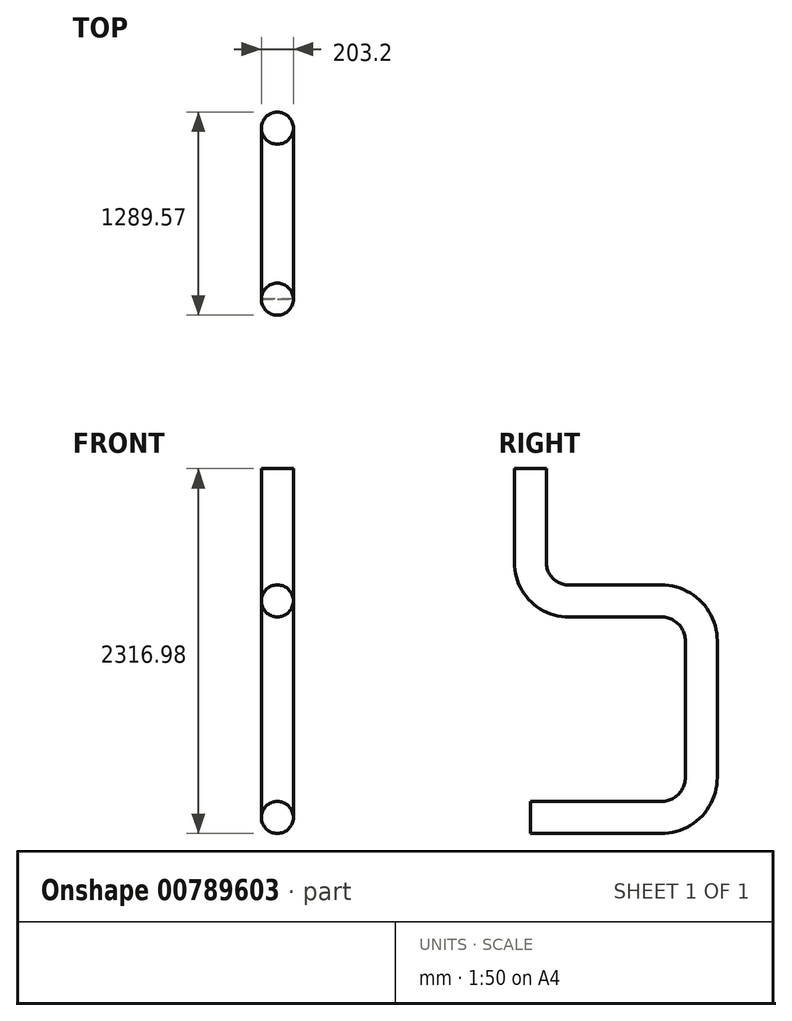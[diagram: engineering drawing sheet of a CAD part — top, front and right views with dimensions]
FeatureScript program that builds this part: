
annotation { "Feature Type Name" : "Feature", "Feature Type Description" : "" }
export const myFeature = defineFeature(function(context is Context, id is Id, definition is map)
    precondition{}
    {
        {
            var Q0;
            Q0=qCreatedBy(makeId("Front.planeOp"),FACE);
            var sketch = newSketch(context, id + "F0", { "sketchPlane" : qUnion([Q0])});
            skCircle(sketch, "E0", {"center": v(0, 0) * mm, "radius": 101.6 * mm});
            skSolve(sketch);
        }
        {
            var Q0;
            Q0=qCreatedBy(makeId("Right.planeOp"),FACE);
            var sketch = newSketch(context, id + "F1", { "sketchPlane" : qUnion([Q0])});
            skLineSegment(sketch, "E1", {"start": v(0, 0) * mm, "end": v(832.37, 0) * mm});
            skLineSegment(sketch, "E2", {"start": v(1086.37, 254) * mm, "end": v(1086.37, 1121.24) * mm});
            skArc(sketch, "E3", {"start": v(832.37, 0) * mm, "mid": v(1011.97, 74.4) * mm, "end": v(1086.37, 254) * mm});
            skPoint(sketch, "E3.first.point", {"position": v(1086.37, 254) * mm});
            skLineSegment(sketch, "E4", {"start": v(832.37, 1375.24) * mm, "end": v(244.31, 1375.24) * mm});
            skArc(sketch, "E5", {"start": v(1086.37, 1121.24) * mm, "mid": v(1011.97, 1300.85) * mm, "end": v(832.37, 1375.24) * mm});
            skPoint(sketch, "E5.first.point", {"position": v(832.37, 1375.24) * mm});
            skPoint(sketch, "E5.second.point", {"position": v(1086.37, 1121.24) * mm});
            skPoint(sketch, "E5.third.point", {"position": v(1086.37, 1121.24) * mm});
            skLineSegment(sketch, "E6", {"start": v(0, 1619.56) * mm, "end": v(0, 2215.38) * mm});
            skArc(sketch, "E7", {"start": v(0, 1619.56) * mm, "mid": v(71.56, 1446.8) * mm, "end": v(244.31, 1375.24) * mm});
            skSolve(sketch);
        }
        {
            var Q0;
            Q0 = qSketchRegion(id + "F0", true);
            var Q1;
            Q1 = qConstructionFilter(qBodyType(qCreatedBy(id + "F1" ,EDGE), BodyType.WIRE), ConstructionObject.NO);
            sweep(context, id + "F2", {"profiles" : qUnion([Q0]), "path" : qUnion([Q1])});
        }
    });
